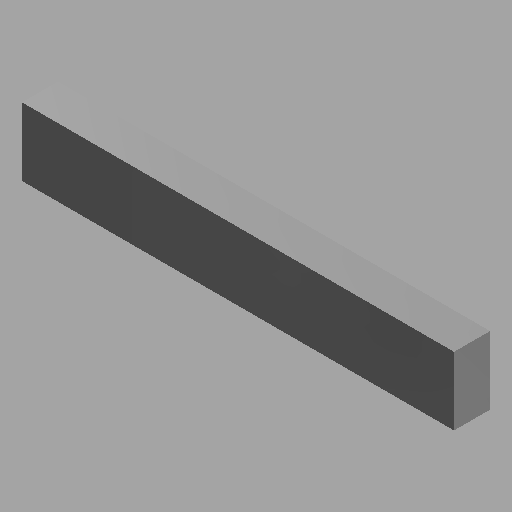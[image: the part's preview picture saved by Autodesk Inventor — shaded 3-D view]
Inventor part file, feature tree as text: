
AUTODESK INVENTOR PART (.ipt)
format: ipt  version: 2023 (Build 270158030, 158C)  size: 95,232 bytes
history: native  units: mm (DEFAULTED — no unit token found)
features: extrude x2, sketch x2
ambient origin geometry x8: Origin, YZ Plane, XZ Plane, XY Plane, X Axis, Y Axis, Z Axis, Center Point
bodies: Solid1 (feature_tree)
feature tree (4):
  extrude  "Extrusion1"  Depth=25.4mm TaperAngle=0.0deg
  extrude  "Extrusion2"  [1 undecoded]
  sketch  "Sketch1"  dims[d0=25.4mm d1=0.0mm d2=25.4mm d3=0.0mm]
  sketch  "Sketch2"
note: 1 required parameter value undecoded (feature->parameter linkage not recoverable at this tier; creation-order binding heuristic only, values carry confidence <= 0.55)
